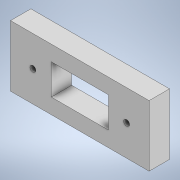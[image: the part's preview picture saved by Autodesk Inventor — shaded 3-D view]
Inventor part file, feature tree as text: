
AUTODESK INVENTOR PART (.ipt)
format: ipt  version: 2022 (Build 260153000, 153)  size: 110,592 bytes
history: native  units: mm
features: extrude x3, sketch x3
ambient origin geometry x8: Origin, YZ Plane, XZ Plane, XY Plane, X Axis, Y Axis, Z Axis, Center Point
bodies: Solid1 (feature_tree)
feature tree (6):
  extrude  "Extrusion1"  Depth=30.0mm
  extrude  "Extrusion2"  Depth=28.0mm
  extrude  "Extrusion3"  Depth=10.0mm TaperAngle=0.0deg
  sketch  "Sketch1"  dims[d0=68.0mm d1=30.0mm]
  sketch  "Sketch2"  dims[d2=10.0mm d3=0.0mm d4=28.0mm]
  sketch  "Sketch3"  dims[d5=15.0mm d6=10.0mm d7=0.0mm d8=2.903mm d9=2.903mm d10=9.0mm d11=9.0mm d12=10.0mm d13=0.0mm]
